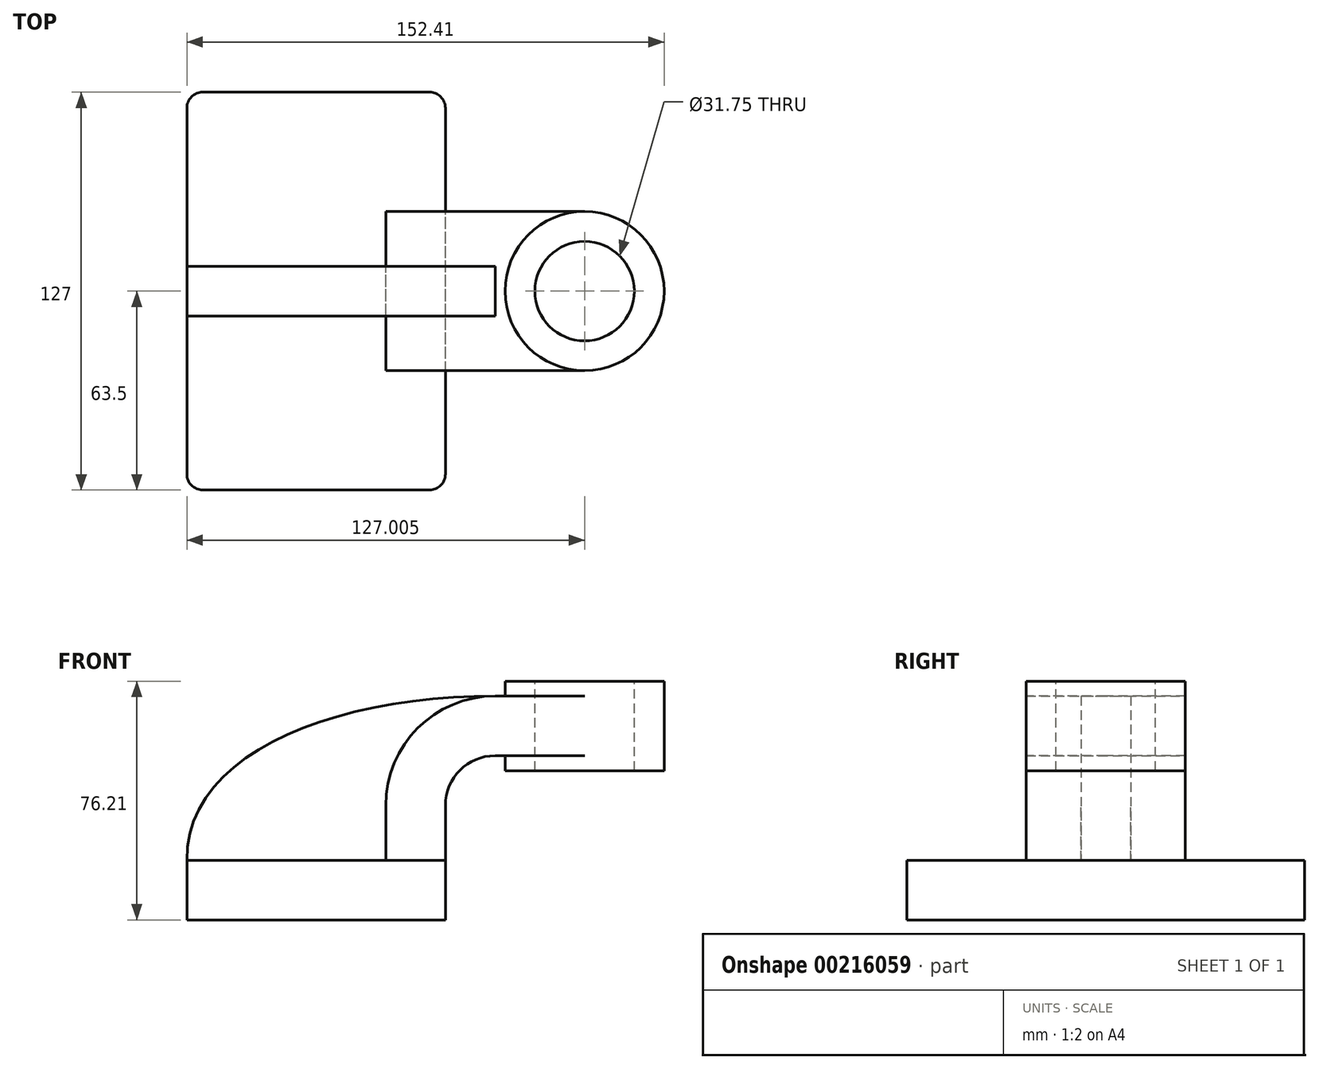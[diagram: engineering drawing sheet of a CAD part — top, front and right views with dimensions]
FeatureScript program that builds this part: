
annotation { "Feature Type Name" : "Feature", "Feature Type Description" : "" }
export const myFeature = defineFeature(function(context is Context, id is Id, definition is map)
    precondition{}
    {
        {
            var Q0;
            Q0=qCreatedBy(makeId("Front.planeOp"),FACE);
            var sketch = newSketch(context, id + "F0", { "sketchPlane" : qUnion([Q0])});
            skLineSegment(sketch, "E0.bottom", {"start": v(-41.28, 9.53) * mm, "end": v(41.28, 9.53) * mm});
            skLineSegment(sketch, "E0.top", {"start": v(-41.28, -9.53) * mm, "end": v(41.28, -9.53) * mm});
            skLineSegment(sketch, "E0.left", {"start": v(-41.28, 9.53) * mm, "end": v(-41.28, -9.53) * mm});
            skLineSegment(sketch, "E0.right", {"start": v(41.28, 9.53) * mm, "end": v(41.28, -9.53) * mm});
            skLineSegment(sketch, "E1.bottom", {"start": v(60.33, 66.67) * mm, "end": v(111.13, 66.67) * mm});
            skLineSegment(sketch, "E1.top", {"start": v(60.33, 38.1) * mm, "end": v(111.13, 38.1) * mm});
            skLineSegment(sketch, "E1.left", {"start": v(60.33, 66.67) * mm, "end": v(60.33, 38.1) * mm});
            skLineSegment(sketch, "E1.right", {"start": v(111.12, 66.67) * mm, "end": v(111.12, 38.1) * mm});
            skLineSegment(sketch, "E2", {"start": v(41.27, 9.53) * mm, "end": v(41.27, 27) * mm});
            skLineSegment(sketch, "E3", {"start": v(57.15, 42.88) * mm, "end": v(85.73, 42.88) * mm});
            skArc(sketch, "E4", {"start": v(57.15, 42.88) * mm, "mid": v(45.92, 38.23) * mm, "end": v(41.28, 27) * mm});
            skPoint(sketch, "E5", {"position": v(85.73, 52.39) * mm});
            skPoint(sketch, "E5.positionSnap0", {"position": v(85.73, 38.1) * mm});
            skPoint(sketch, "E6", {"position": v(85.73, 42.88) * mm});
            skLineSegment(sketch, "E7.0", {"start": v(57.15, 61.93) * mm, "end": v(85.73, 61.93) * mm});
            skArc(sketch, "E7.1", {"start": v(57.15, 61.93) * mm, "mid": v(32.45, 51.7) * mm, "end": v(22.23, 27) * mm});
            skLineSegment(sketch, "E7.2", {"start": v(22.23, 9.53) * mm, "end": v(22.23, 27) * mm});
            skLineSegment(sketch, "E8", {"start": v(85.73, 38.1) * mm, "end": v(85.73, 66.67) * mm});
            skFitSpline(sketch, "E9", {"points": [v(57.15, 61.93) * mm, v(-41.28, 9.52) * mm], "startDerivative": vector(-154.54, 0.4) * mm, "endDerivative": vector(1.74, -101.39) * mm});
            skSolve(sketch);
        }
        {
            var Q0;
            Q0=makeQuery(id+"F0.imprint","IMPRINT",FACE,{"disambiguationData":[TD([[makeQuery(id+"F0.imprint","IMPRINT",EDGE,{"derivedFrom":sQuery(id+"F0.wireOp",EDGE,"E0.top")}),1.0]])]});
            extrude(context, id + "F1", {"entities" : qUnion([Q0]), "endBound" : BoundingType.SYMMETRIC, "depth" : 127 * mm});
        }
        {
            var Q0;
            {var subQ0=sQuery(id+"F0.wireOp",EDGE,"E7.0");var subQ1=sQuery(id+"F0.wireOp",EDGE,"E1.left");var subQ2=makeQuery(id+"F0.imprint","INTERSECT",VERTEX,{"derivedFrom":[subQ1,subQ0]});Q0=makeQuery(id+"F0.imprint","IMPRINT",FACE,{"disambiguationData":[TD([[makeQuery(id+"F0.imprint","IMPRINT",EDGE,{"disambiguationData":[TD([[subQ2,-1.0]])],"derivedFrom":subQ1}),1.0]])]});}
            var Q1;
            {var subQ4=sQuery(id+"F0.wireOp",EDGE,"E2");Q1=makeQuery(id+"F0.imprint","IMPRINT",FACE,{"disambiguationData":[TD([[makeQuery(id+"F0.imprint","IMPRINT",EDGE,{"derivedFrom":subQ4}),1.0]])]});}
            extrude(context, id + "F2", {"entities" : qUnion([Q0, Q1]), "endBound" : BoundingType.SYMMETRIC, "depth" : 50.8 * mm});
        }
        {
            var Q0;
            Q0=makeQuery(id+"F0.imprint","IMPRINT",FACE,{"disambiguationData":[TD([[makeQuery(id+"F0.imprint","IMPRINT",EDGE,{"derivedFrom":sQuery(id+"F0.wireOp",EDGE,"E7.1")}),-1.0]])]});
            extrude(context, id + "F3", {"entities" : qUnion([Q0]), "endBound" : BoundingType.SYMMETRIC, "depth" : 15.88 * mm});
        }
        {
            var Q0;
            {var subQ0=sQuery(id+"F0.wireOp",EDGE,"E1.right");Q0=makeQuery(id+"F0.imprint","IMPRINT",FACE,{"disambiguationData":[TD([[makeQuery(id+"F0.imprint","IMPRINT",EDGE,{"derivedFrom":subQ0}),-1.0]])]});}
            var Q1;
            Q1=sQuery(id+"F0.wireOp",EDGE,"E8");
            revolve(context, id + "F4", {"operationType" : NewBodyOperationType.ADD, "entities" : qUnion([Q0]), "axis" : qUnion([Q1]), "revolveType" : RevolveType.FULL});
        }
        {
            var Q0;
            Q0=makeQuery(id+"F1.opExtrude","CAP_EDGE",EDGE,{"disambiguationData":[OSD([sQuery(id+"F0.wireOp",EDGE,"E0.right")])],"isStart":false});
            var Q1;
            Q1=makeQuery(id+"F1.opExtrude","CAP_EDGE",EDGE,{"disambiguationData":[OSD([sQuery(id+"F0.wireOp",EDGE,"E0.left")])],"isStart":false});
            var Q2;
            Q2=makeQuery(id+"F1.opExtrude","CAP_EDGE",EDGE,{"disambiguationData":[OSD([sQuery(id+"F0.wireOp",EDGE,"E0.left")])],"isStart":true});
            var Q3;
            Q3=makeQuery(id+"F1.opExtrude","CAP_EDGE",EDGE,{"disambiguationData":[OSD([sQuery(id+"F0.wireOp",EDGE,"E0.right")])],"isStart":true});
            fillet(context, id + "F5", {"entities" : qUnion([Q0, Q1, Q2, Q3]), "radius" : 5.08 * mm, "tangentPropagation" : true, "allowEdgeOverflow" : false});
        }
        {
            var Q0;
            Q0=makeQuery(id+"F4.opRevolve","SWEPT_FACE",FACE,{"disambiguationData":[OSD([sQuery(id+"F0.wireOp",EDGE,"E1.bottom")])]});
            var sketch = newSketch(context, id + "F6", { "sketchPlane" : qUnion([Q0])});
            skCircle(sketch, "E10", {"center": v(85.73, 0) * mm, "radius": 15.88 * mm});
            skSolve(sketch);
        }
        {
            var Q0;
            Q0 = qSketchRegion(id + "F6", true);
            extrude(context, id + "F7", {"entities" : qUnion([Q0]), "operationType" : NewBodyOperationType.ADD, "depth" : 25.4 * mm});
        }
        {
            var Q0;
            Q0=makeQuery(id+"F7.opExtrude","CAP_FACE",FACE,{"disambiguationData":[OSD([sQuery(id+"F6.wireOp",EDGE,"E10")])],"isStart":false});
            extrude(context, id + "F8", {"entities" : qUnion([Q0]), "operationType" : NewBodyOperationType.REMOVE, "endBound" : BoundingType.THROUGH_ALL, "oppositeDirection" : true, "depth" : 25.4 * mm});
        }
    });
